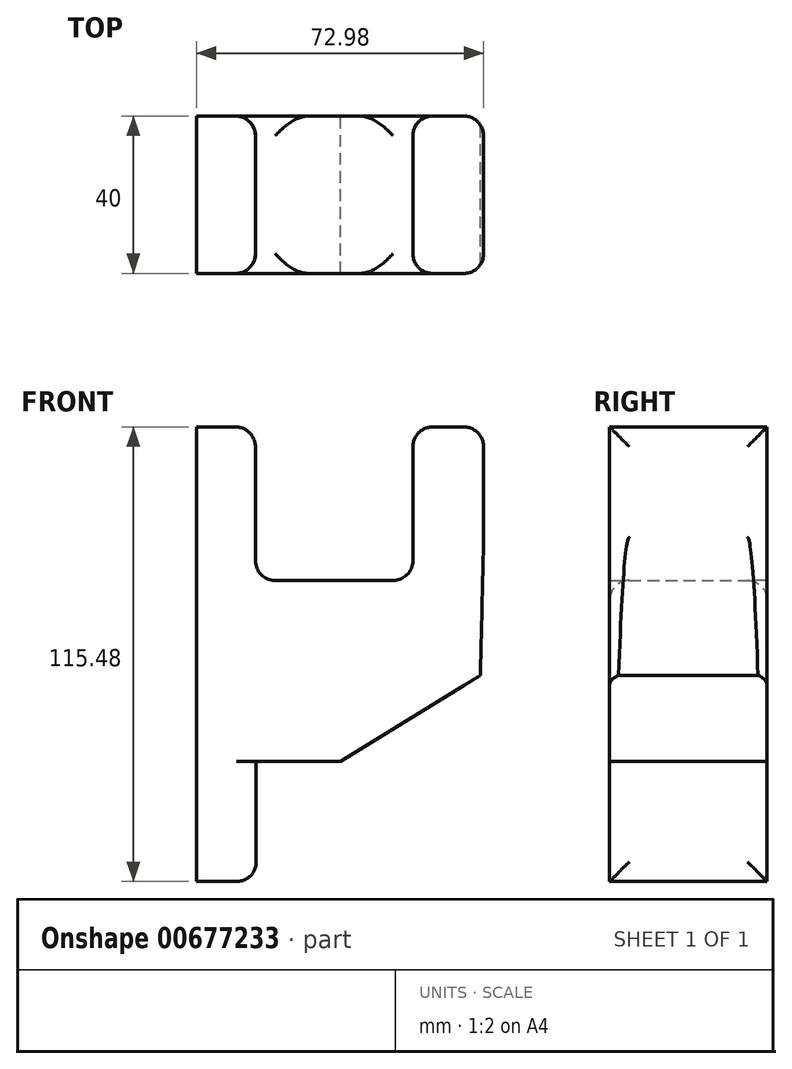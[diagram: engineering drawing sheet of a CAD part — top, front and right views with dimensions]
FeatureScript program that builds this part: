
annotation { "Feature Type Name" : "Feature", "Feature Type Description" : "" }
export const myFeature = defineFeature(function(context is Context, id is Id, definition is map)
    precondition{}
    {
        {
            var Q0;
            Q0=qCreatedBy(makeId("Front.planeOp"),FACE);
            var sketch = newSketch(context, id + "F0", { "sketchPlane" : qUnion([Q0])});
            skLineSegment(sketch, "E0.bottom", {"start": v(-60.78, 28.09) * mm, "end": v(-45.78, 28.09) * mm});
            skLineSegment(sketch, "E0.left", {"start": v(-60.78, 28.09) * mm, "end": v(-60.78, -56.91) * mm});
            skLineSegment(sketch, "E0.right", {"start": v(-45.78, 28.09) * mm, "end": v(-45.78, -56.91) * mm});
            skLineSegment(sketch, "E1", {"start": v(12.2, 0) * mm, "end": v(12.2, 28.09) * mm});
            skLineSegment(sketch, "E2", {"start": v(12.2, 28.09) * mm, "end": v(-5.78, 28.09) * mm});
            skLineSegment(sketch, "E3", {"start": v(-5.78, 28.09) * mm, "end": v(-5.78, 0) * mm});
            skLineSegment(sketch, "E4.bottom", {"start": v(-45.78, -56.91) * mm, "end": v(-45.57, -56.91) * mm});
            skLineSegment(sketch, "E4.top", {"start": v(-60.78, -87.39) * mm, "end": v(-45.57, -87.39) * mm});
            skLineSegment(sketch, "E4.left", {"start": v(-60.78, -56.91) * mm, "end": v(-60.78, -87.39) * mm});
            skLineSegment(sketch, "E4.right", {"start": v(-45.57, -56.91) * mm, "end": v(-45.57, -87.39) * mm});
            skPoint(sketch, "E5.end.orphan", {"position": v(-45.78, 0) * mm});
            skLineSegment(sketch, "E6", {"start": v(-45.78, -10.9) * mm, "end": v(-5.78, -10.9) * mm});
            skLineSegment(sketch, "E7", {"start": v(-5.78, -10.9) * mm, "end": v(-5.78, 0) * mm});
            skPoint(sketch, "E8.end.orphan", {"position": v(0, -35.02) * mm});
            skLineSegment(sketch, "E9", {"start": v(-45.57, -56.91) * mm, "end": v(-24.14, -56.91) * mm});
            skLineSegment(sketch, "E10", {"start": v(11.4, -35.02) * mm, "end": v(12.2, 0) * mm});
            skLineSegment(sketch, "E11", {"start": v(-24.14, -56.91) * mm, "end": v(11.4, -35.02) * mm});
            skSolve(sketch);
        }
        {
            var Q0;
            {var subQ1=sQuery(id+"F0.wireOp",EDGE,"E0.bottom");Q0=makeQuery(id+"F0.imprint","IMPRINT",FACE,{"disambiguationData":[TD([[makeQuery(id+"F0.imprint","IMPRINT",EDGE,{"derivedFrom":subQ1}),-1.0]])]});}
            var Q1;
            {var subQ0=sQuery(id+"F0.wireOp",EDGE,"E8");Q1=makeQuery(id+"F0.imprint","IMPRINT",FACE,{"disambiguationData":[TD([[makeQuery(id+"F0.imprint","IMPRINT",EDGE,{"derivedFrom":subQ0}),1.0]])]});}
            var Q2;
            Q2=makeQuery(id+"F0.imprint","IMPRINT",FACE,{"disambiguationData":[TD([[makeQuery(id+"F0.imprint","IMPRINT",EDGE,{"derivedFrom":sQuery(id+"F0.wireOp",EDGE,"E1")}),1.0]])]});
            extrude(context, id + "F1", {"entities" : qUnion([Q0, Q1, Q2]), "depth" : 40 * mm, "offsetDistance" : 25 * mm});
        }
        {
            var Q0;
            Q0=makeQuery(id+"F1.opExtrude","SWEPT_FACE",FACE,{"disambiguationData":[OSD([sQuery(id+"F0.wireOp",EDGE,"E5")])]});
            var Q1;
            Q1=makeQuery(id+"F1.opExtrude","SWEPT_FACE",FACE,{"disambiguationData":[OSD([sQuery(id+"F0.wireOp",EDGE,"E0.right")])]});
            var Q2;
            Q2=makeQuery(id+"F1.opExtrude","SWEPT_FACE",FACE,{"disambiguationData":[OSD([sQuery(id+"F0.wireOp",EDGE,"E3")])]});
            var Q3;
            Q3=makeQuery(id+"F1.opExtrude","SWEPT_FACE",FACE,{"disambiguationData":[OSD([sQuery(id+"F0.wireOp",EDGE,"Q3dAqKJx-VZWt-uSki-c0VF-OdjLQpaGzlug")])]});
            var Q4;
            Q4=makeQuery(id+"F1.opExtrude","SWEPT_FACE",FACE,{"disambiguationData":[OSD([sQuery(id+"F0.wireOp",EDGE,"E1")])]});
            var Q5;
            Q5=makeQuery(id+"F1.opExtrude","CAP_EDGE",EDGE,{"disambiguationData":[OSD([sQuery(id+"F0.wireOp",EDGE,"E4.right")])],"isStart":false});
            var Q6;
            Q6=makeQuery(id+"F1.opExtrude","CAP_EDGE",EDGE,{"disambiguationData":[OSD([sQuery(id+"F0.wireOp",EDGE,"E4.right")])],"isStart":true});
            var Q7;
            Q7=makeQuery(id+"F1.opExtrude","SWEPT_EDGE",EDGE,{"disambiguationData":[OSD([sQuery(id+"F0.wireOp",EDGE,"E4.top"),sQuery(id+"F0.wireOp",EDGE,"E4.right")])]});
            fillet(context, id + "F2", {"entities" : qUnion([Q0, Q1, Q2, Q3, Q4, Q5, Q6, Q7]), "radius" : 5 * mm, "tangentPropagation" : true, "allowEdgeOverflow" : false});
        }
    });
